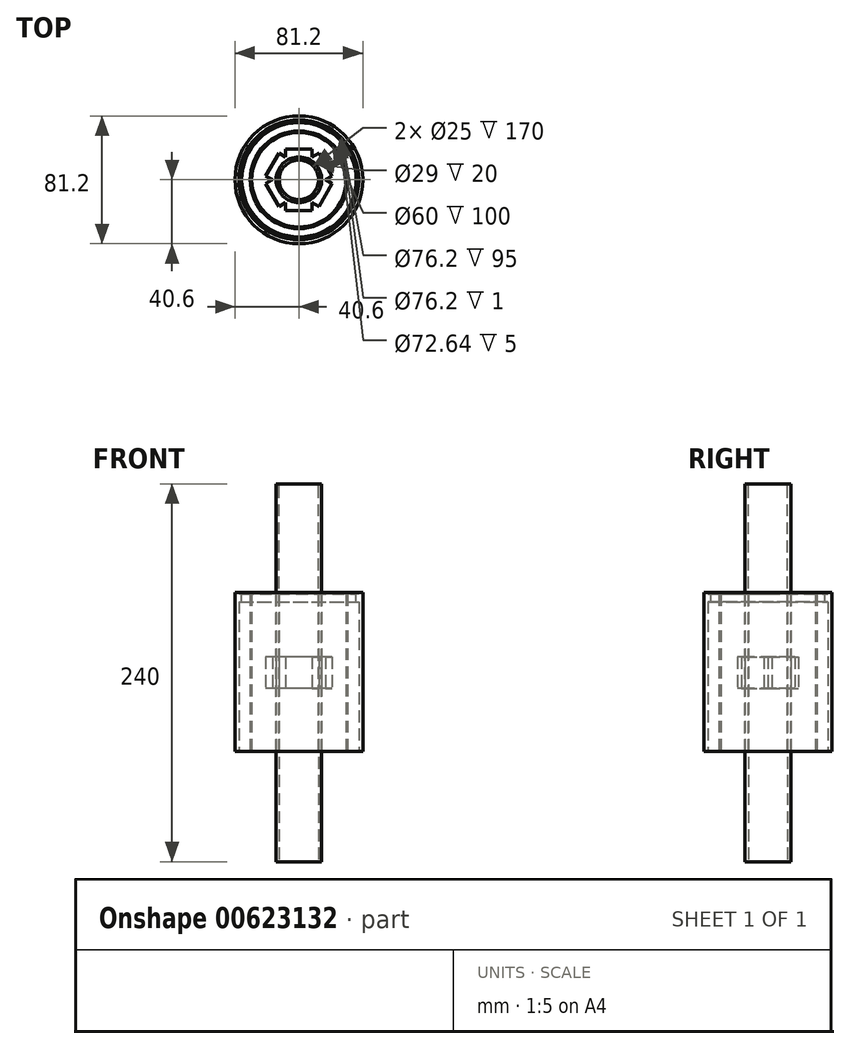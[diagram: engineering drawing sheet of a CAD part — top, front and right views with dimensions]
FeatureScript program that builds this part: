
annotation { "Feature Type Name" : "Feature", "Feature Type Description" : "" }
export const myFeature = defineFeature(function(context is Context, id is Id, definition is map)
    precondition{}
    {
        {
            var Q0;
            Q0=qCreatedBy(makeId("Top.planeOp"),FACE);
            var sketch = newSketch(context, id + "F0", { "sketchPlane" : qUnion([Q0])});
            skCircle(sketch, "E0", {"center": v(0, 0) * mm, "radius": 12.5 * mm});
            skCircle(sketch, "E1", {"center": v(0, 0) * mm, "radius": 30 * mm});
            skCircle(sketch, "E2", {"center": v(0, 0) * mm, "radius": 38.1 * mm});
            skCircle(sketch, "E3.0", {"center": v(0, 0) * mm, "radius": 14.5 * mm});
            skCircle(sketch, "E4.0", {"center": v(0, 0) * mm, "radius": 31 * mm});
            skCircle(sketch, "E5.0", {"center": v(0, 0) * mm, "radius": 40.6 * mm});
            skSolve(sketch);
        }
        {
            var Q0;
            Q0=makeQuery(id+"F0.imprint","IMPRINT",FACE,{"disambiguationData":[TD([[makeQuery(id+"F0.imprint","IMPRINT",EDGE,{"derivedFrom":sQuery(id+"F0.wireOp",EDGE,"E0")}),-1.0]])]});
            var Q1;
            Q1=makeQuery(id+"F0.imprint","IMPRINT",FACE,{"disambiguationData":[TD([[makeQuery(id+"F0.imprint","IMPRINT",EDGE,{"derivedFrom":sQuery(id+"F0.wireOp",EDGE,"E1")}),-1.0]])]});
            var Q2;
            Q2=makeQuery(id+"F0.imprint","IMPRINT",FACE,{"disambiguationData":[TD([[makeQuery(id+"F0.imprint","IMPRINT",EDGE,{"derivedFrom":sQuery(id+"F0.wireOp",EDGE,"E2")}),-1.0]])]});
            extrude(context, id + "F1", {"entities" : qUnion([Q0, Q1, Q2]), "depth" : 100 * mm, "symmetric" : true});
        }
        {
            var Q0;
            Q0=qCreatedBy(makeId("Top.planeOp"),FACE);
            var sketch = newSketch(context, id + "F2", { "sketchPlane" : qUnion([Q0])});
            skCircle(sketch, "E6.0", {"center": v(0, 0) * mm, "radius": 14.5 * mm});
            skCircle(sketch, "E7.cCircle", {"center": v(0, 0) * mm, "radius": 14.5 * mm, "construction": true});
            skLineSegment(sketch, "E7.0", {"start": v(-8.37, 14.5) * mm, "end": v(8.37, 14.5) * mm, "construction": true});
            skLineSegment(sketch, "E7.1", {"start": v(8.37, 14.5) * mm, "end": v(16.74, 0) * mm, "construction": true});
            skLineSegment(sketch, "E7.2", {"start": v(16.74, 0) * mm, "end": v(8.37, -14.5) * mm, "construction": true});
            skLineSegment(sketch, "E7.3", {"start": v(8.37, -14.5) * mm, "end": v(-8.37, -14.5) * mm, "construction": true});
            skLineSegment(sketch, "E7.4", {"start": v(-8.37, -14.5) * mm, "end": v(-16.74, 0) * mm, "construction": true});
            skLineSegment(sketch, "E7.5", {"start": v(-16.74, 0) * mm, "end": v(-8.37, 14.5) * mm, "construction": true});
            skPoint(sketch, "E7.0.midPoint", {"position": v(0, 14.5) * mm});
            skLineSegment(sketch, "E8.bottom", {"start": v(-8.37, 14.5) * mm, "end": v(8.37, 14.5) * mm});
            skLineSegment(sketch, "E8.top", {"start": v(-8.37, 19.5) * mm, "end": v(8.37, 19.5) * mm});
            skLineSegment(sketch, "E8.left", {"start": v(-8.37, 14.5) * mm, "end": v(-8.37, 19.5) * mm});
            skLineSegment(sketch, "E8.right", {"start": v(8.37, 14.5) * mm, "end": v(8.37, 19.5) * mm});
            skLineSegment(sketch, "E9.1.0", {"start": v(12.7, 17) * mm, "end": v(21.07, 2.5) * mm});
            skLineSegment(sketch, "E9.1.1", {"start": v(8.37, 14.5) * mm, "end": v(12.7, 17) * mm});
            skLineSegment(sketch, "E9.1.2", {"start": v(16.74, 0) * mm, "end": v(21.07, 2.5) * mm});
            skLineSegment(sketch, "E9.2.0", {"start": v(21.07, -2.5) * mm, "end": v(12.7, -17) * mm});
            skLineSegment(sketch, "E9.2.1", {"start": v(16.74, 0) * mm, "end": v(21.07, -2.5) * mm});
            skLineSegment(sketch, "E9.2.2", {"start": v(8.37, -14.5) * mm, "end": v(12.7, -17) * mm});
            skLineSegment(sketch, "E9.3.0", {"start": v(8.37, -19.5) * mm, "end": v(-8.37, -19.5) * mm});
            skLineSegment(sketch, "E9.3.1", {"start": v(8.37, -14.5) * mm, "end": v(8.37, -19.5) * mm});
            skLineSegment(sketch, "E9.3.2", {"start": v(-8.37, -14.5) * mm, "end": v(-8.37, -19.5) * mm});
            skLineSegment(sketch, "E9.4.0", {"start": v(-12.7, -17) * mm, "end": v(-21.07, -2.5) * mm});
            skLineSegment(sketch, "E9.4.1", {"start": v(-8.37, -14.5) * mm, "end": v(-12.7, -17) * mm});
            skLineSegment(sketch, "E9.4.2", {"start": v(-16.74, 0) * mm, "end": v(-21.07, -2.5) * mm});
            skLineSegment(sketch, "E9.5.0", {"start": v(-21.07, 2.5) * mm, "end": v(-12.7, 17) * mm});
            skLineSegment(sketch, "E9.5.1", {"start": v(-16.74, 0) * mm, "end": v(-21.07, 2.5) * mm});
            skLineSegment(sketch, "E9.5.2", {"start": v(-8.37, 14.5) * mm, "end": v(-12.7, 17) * mm});
            skLineSegment(sketch, "E9.anchor1", {"start": v(0, 0) * mm, "end": v(-8.37, 19.5) * mm, "construction": true});
            skLineSegment(sketch, "E9.anchor2", {"start": v(0, 0) * mm, "end": v(-21.07, 2.5) * mm, "construction": true});
            skLineSegment(sketch, "E10", {"start": v(-8.37, 14.5) * mm, "end": v(-16.74, 0) * mm});
            skLineSegment(sketch, "E11", {"start": v(-8.37, -14.5) * mm, "end": v(8.37, -14.5) * mm});
            skLineSegment(sketch, "E12", {"start": v(8.37, -14.5) * mm, "end": v(16.74, 0) * mm});
            skLineSegment(sketch, "E13", {"start": v(16.74, 0) * mm, "end": v(8.37, 14.5) * mm});
            skLineSegment(sketch, "E14", {"start": v(-16.74, 0) * mm, "end": v(-8.37, -14.5) * mm});
            skSolve(sketch);
        }
        {
            var Q0;
            Q0=makeQuery(id+"F2.imprint","IMPRINT",FACE,{"disambiguationData":[TD([[makeQuery(id+"F2.imprint","IMPRINT",EDGE,{"derivedFrom":sQuery(id+"F2.wireOp",EDGE,"E9.5.0")}),-1.0]])]});
            var Q1;
            Q1=makeQuery(id+"F2.imprint","IMPRINT",FACE,{"disambiguationData":[TD([[makeQuery(id+"F2.imprint","IMPRINT",EDGE,{"derivedFrom":sQuery(id+"F2.wireOp",EDGE,"E8.top")}),-1.0]])]});
            var Q2;
            Q2=makeQuery(id+"F2.imprint","IMPRINT",FACE,{"disambiguationData":[TD([[makeQuery(id+"F2.imprint","IMPRINT",EDGE,{"derivedFrom":sQuery(id+"F2.wireOp",EDGE,"E9.1.0")}),-1.0]])]});
            var Q3;
            Q3=makeQuery(id+"F2.imprint","IMPRINT",FACE,{"disambiguationData":[TD([[makeQuery(id+"F2.imprint","IMPRINT",EDGE,{"derivedFrom":sQuery(id+"F2.wireOp",EDGE,"E9.2.0")}),-1.0]])]});
            var Q4;
            Q4=makeQuery(id+"F2.imprint","IMPRINT",FACE,{"disambiguationData":[TD([[makeQuery(id+"F2.imprint","IMPRINT",EDGE,{"derivedFrom":sQuery(id+"F2.wireOp",EDGE,"E9.3.0")}),-1.0]])]});
            var Q5;
            Q5=makeQuery(id+"F2.imprint","IMPRINT",FACE,{"disambiguationData":[TD([[makeQuery(id+"F2.imprint","IMPRINT",EDGE,{"derivedFrom":sQuery(id+"F2.wireOp",EDGE,"E9.4.0")}),-1.0]])]});
            var Q6;
            {var subQ0=sQuery(id+"F2.wireOp",EDGE,"E8.bottom");var subQ1=sQuery(id+"F2.wireOp",EDGE,"E6.0");var subQ2=makeQuery(id+"F2.imprint","INTERSECT",VERTEX,{"derivedFrom":[subQ1,subQ0]});Q6=makeQuery(id+"F2.imprint","IMPRINT",FACE,{"disambiguationData":[TD([[makeQuery(id+"F2.imprint","IMPRINT",EDGE,{"disambiguationData":[TD([[subQ2,-1.0]])],"derivedFrom":subQ1}),-1.0]])]});}
            var Q7;
            {var subQ0=sQuery(id+"F2.wireOp",EDGE,"E10");var subQ1=sQuery(id+"F2.wireOp",EDGE,"E6.0");var subQ2=makeQuery(id+"F2.imprint","INTERSECT",VERTEX,{"derivedFrom":[subQ1,subQ0]});Q7=makeQuery(id+"F2.imprint","IMPRINT",FACE,{"disambiguationData":[TD([[makeQuery(id+"F2.imprint","IMPRINT",EDGE,{"disambiguationData":[TD([[subQ2,-1.0]])],"derivedFrom":subQ1}),-1.0]])]});}
            var Q8;
            {var subQ0=sQuery(id+"F2.wireOp",EDGE,"E14");var subQ1=sQuery(id+"F2.wireOp",EDGE,"E6.0");var subQ2=makeQuery(id+"F2.imprint","INTERSECT",VERTEX,{"derivedFrom":[subQ1,subQ0]});Q8=makeQuery(id+"F2.imprint","IMPRINT",FACE,{"disambiguationData":[TD([[makeQuery(id+"F2.imprint","IMPRINT",EDGE,{"disambiguationData":[TD([[subQ2,-1.0]])],"derivedFrom":subQ1}),-1.0]])]});}
            var Q9;
            {var subQ0=sQuery(id+"F2.wireOp",EDGE,"E11");var subQ1=sQuery(id+"F2.wireOp",EDGE,"E6.0");var subQ2=makeQuery(id+"F2.imprint","INTERSECT",VERTEX,{"derivedFrom":[subQ1,subQ0]});Q9=makeQuery(id+"F2.imprint","IMPRINT",FACE,{"disambiguationData":[TD([[makeQuery(id+"F2.imprint","IMPRINT",EDGE,{"disambiguationData":[TD([[subQ2,-1.0]])],"derivedFrom":subQ1}),-1.0]])]});}
            var Q10;
            {var subQ0=sQuery(id+"F2.wireOp",EDGE,"E13");var subQ1=sQuery(id+"F2.wireOp",EDGE,"E6.0");var subQ2=makeQuery(id+"F2.imprint","INTERSECT",VERTEX,{"derivedFrom":[subQ1,subQ0]});Q10=makeQuery(id+"F2.imprint","IMPRINT",FACE,{"disambiguationData":[TD([[makeQuery(id+"F2.imprint","IMPRINT",EDGE,{"disambiguationData":[TD([[subQ2,1.0]])],"derivedFrom":subQ1}),-1.0]])]});}
            var Q11;
            {var subQ0=sQuery(id+"F2.wireOp",EDGE,"E8.bottom");var subQ1=sQuery(id+"F2.wireOp",EDGE,"E6.0");var subQ2=makeQuery(id+"F2.imprint","INTERSECT",VERTEX,{"derivedFrom":[subQ1,subQ0]});Q11=makeQuery(id+"F2.imprint","IMPRINT",FACE,{"disambiguationData":[TD([[makeQuery(id+"F2.imprint","IMPRINT",EDGE,{"disambiguationData":[TD([[subQ2,1.0]])],"derivedFrom":subQ1}),-1.0]])]});}
            extrude(context, id + "F3", {"entities" : qUnion([Q0, Q1, Q2, Q3, Q4, Q5, Q6, Q7, Q8, Q9, Q10, Q11]), "depth" : 20 * mm, "symmetric" : true});
        }
        {
            var Q0;
            Q0=makeQuery(id+"F1.opExtrude","CAP_FACE",FACE,{"disambiguationData":[OSD([sQuery(id+"F0.wireOp",EDGE,"E0"),sQuery(id+"F0.wireOp",EDGE,"E3.0")])],"isStart":false});
            var Q1;
            Q1=qSketchRegion(id+"F5",true);
            extrude(context, id + "F4", {"entities" : qUnion([Q0, Q1]), "operationType" : NewBodyOperationType.ADD, "oppositeDirection" : true, "depth" : 25 * mm});
        }
        {
            var Q0;
            Q0=makeQuery(id+"F1.opExtrude","CAP_FACE",FACE,{"disambiguationData":[OSD([sQuery(id+"F0.wireOp",EDGE,"E2"),sQuery(id+"F0.wireOp",EDGE,"E5.0")])],"isStart":false});
            var sketch = newSketch(context, id + "F5", { "sketchPlane" : qUnion([Q0])});
            skCircle(sketch, "E15.0", {"center": v(0, 0) * mm, "radius": 40.6 * mm});
            skCircle(sketch, "E16", {"center": v(0, 0) * mm, "radius": 14.5 * mm});
            skSolve(sketch);
        }
        {
            var Q0;
            Q0=makeQuery(id+"F5.imprint","IMPRINT",FACE,{"disambiguationData":[TD([[makeQuery(id+"F5.imprint","IMPRINT",EDGE,{"derivedFrom":sQuery(id+"F5.wireOp",EDGE,"E16")}),1.0]])]});
            var Q1;
            Q1=makeQuery(id+"F5.imprint","IMPRINT",FACE,{"disambiguationData":[TD([[makeQuery(id+"F5.imprint","IMPRINT",EDGE,{"derivedFrom":sQuery(id+"F5.wireOp",EDGE,"E15.0")}),1.0]])]});
            var Q2;
            Q2=qSketchRegion(id+"F7",true);
            extrude(context, id + "F6", {"entities" : qUnion([Q0, Q1, Q2]), "depth" : 1 * mm});
        }
        {
            var Q0;
            Q0=makeQuery(id+"F6.opExtrude","CAP_FACE",FACE,{"disambiguationData":[OSD([sQuery(id+"F5.wireOp",EDGE,"E15.0"),sQuery(id+"F5.wireOp",EDGE,"E16")])],"isStart":true});
            var sketch = newSketch(context, id + "F7", { "sketchPlane" : qUnion([Q0])});
            skCircle(sketch, "E17", {"center": v(0, 0) * mm, "radius": 38.63 * mm});
            skCircle(sketch, "E18", {"center": v(0, 0) * mm, "radius": 36.32 * mm});
            skSolve(sketch);
        }
        {
            var Q0;
            Q0=makeQuery(id+"F7.imprint","IMPRINT",FACE,{"disambiguationData":[TD([[makeQuery(id+"F7.imprint","IMPRINT",EDGE,{"derivedFrom":sQuery(id+"F7.wireOp",EDGE,"E17")}),1.0]])]});
            extrude(context, id + "F8", {"entities" : qUnion([Q0]), "operationType" : NewBodyOperationType.ADD, "depth" : 5 * mm});
        }
        {
            var Q0;
            Q0=makeQuery(id+"F1.opExtrude","CAP_FACE",FACE,{"disambiguationData":[OSD([sQuery(id+"F0.wireOp",EDGE,"E0"),sQuery(id+"F0.wireOp",EDGE,"E3.0")])],"isStart":true});
            extrude(context, id + "F9", {"entities" : qUnion([Q0]), "operationType" : NewBodyOperationType.ADD, "depth" : 70 * mm, "offsetDistance" : 25 * mm});
        }
        {
            var Q0;
            Q0=makeQuery(id+"F1.opExtrude","SWEPT_BODY",BODY,{"disambiguationData":[OSD([sQuery(id+"F0.wireOp",EDGE,"E0"),sQuery(id+"F0.wireOp",EDGE,"E3.0")])]});
            var Q1;
            Q1=qCreatedBy(makeId("Top.planeOp"),FACE);
            mirror(context, id + "F10", {"entities" : qUnion([Q0]), "mirrorPlane" : qUnion([Q1])});
        }
    });
